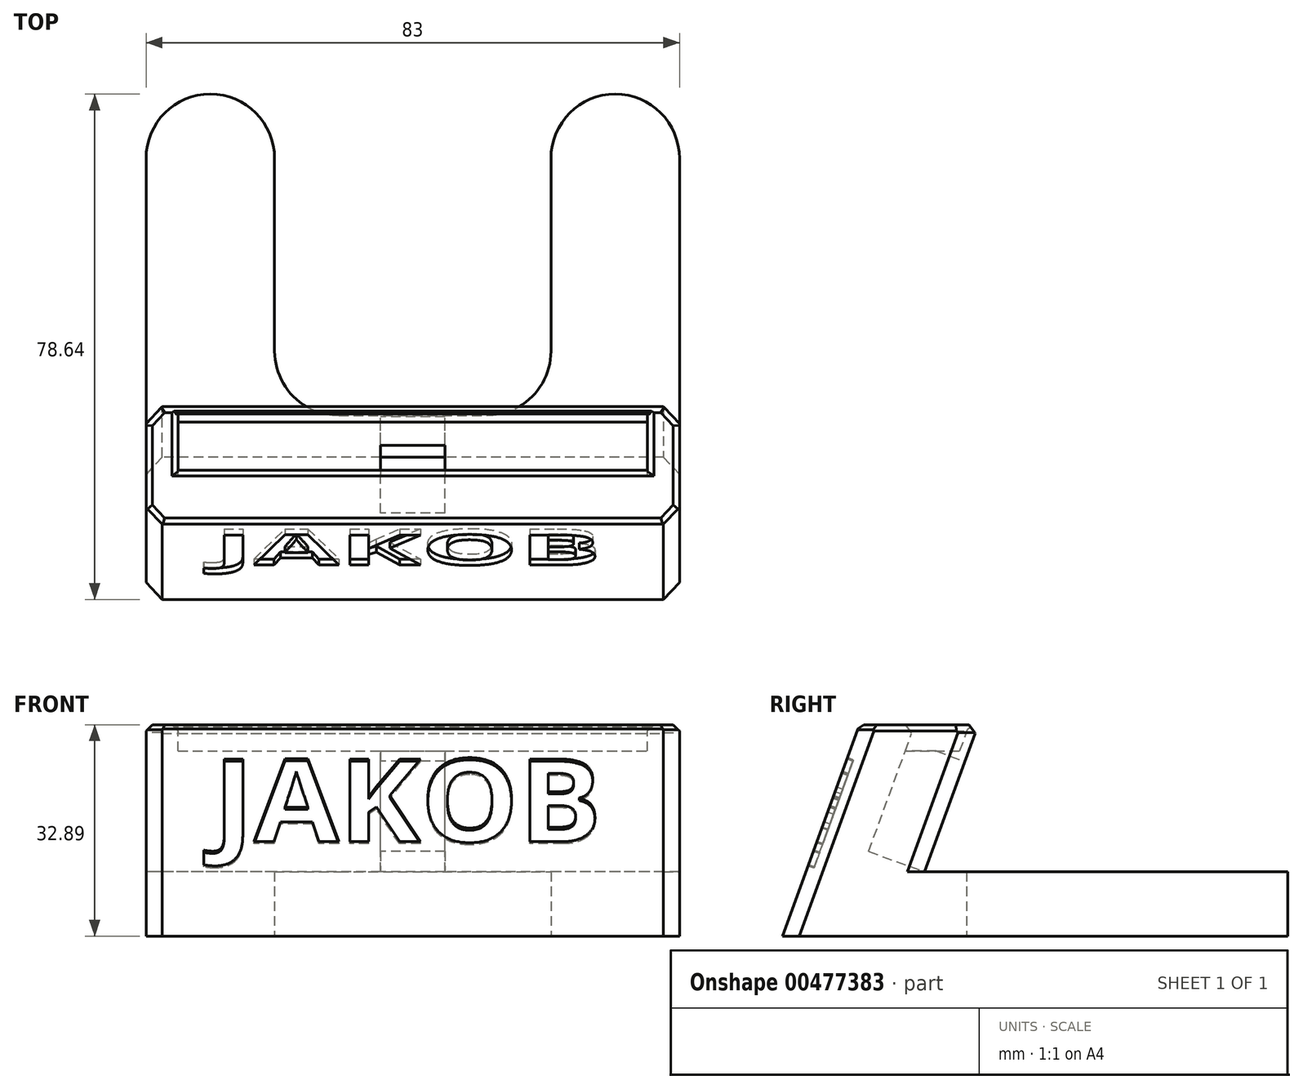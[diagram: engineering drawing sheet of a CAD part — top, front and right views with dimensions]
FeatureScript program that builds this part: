
annotation { "Feature Type Name" : "Feature", "Feature Type Description" : "" }
export const myFeature = defineFeature(function(context is Context, id is Id, definition is map)
    precondition{}
    {
        {
            var Q0;
            Q0=qCreatedBy(makeId("Top.planeOp"),FACE);
            var sketch = newSketch(context, id + "F0", { "sketchPlane" : qUnion([Q0])});
            skLineSegment(sketch, "E0.bottom", {"start": v(0, 0) * mm, "end": v(83, 0) * mm});
            skLineSegment(sketch, "E0.left", {"start": v(0, 0) * mm, "end": v(0, 75) * mm});
            skLineSegment(sketch, "E0.right", {"start": v(83, 0) * mm, "end": v(83, 75) * mm});
            skLineSegment(sketch, "E1", {"start": v(0, 75) * mm, "end": v(20, 75) * mm});
            skLineSegment(sketch, "E2", {"start": v(20, 75) * mm, "end": v(20, 25) * mm});
            skLineSegment(sketch, "E3", {"start": v(20, 25) * mm, "end": v(63, 25) * mm});
            skLineSegment(sketch, "E4", {"start": v(63, 25) * mm, "end": v(63, 75) * mm});
            skLineSegment(sketch, "E5", {"start": v(63, 75) * mm, "end": v(83, 75) * mm});
            skSolve(sketch);
        }
        {
            var Q0;
            Q0 = qSketchRegion(id + "F0", true);
            extrude(context, id + "F1", {"entities" : qUnion([Q0]), "depth" : 10 * mm});
        }
        {
            var Q0;
            Q0=makeQuery(id+"F1.opExtrude","CAP_FACE",FACE,{"disambiguationData":[OSD([sQuery(id+"F0.wireOp",EDGE,"E0.bottom"),sQuery(id+"F0.wireOp",EDGE,"E0.left"),sQuery(id+"F0.wireOp",EDGE,"E0.right"),sQuery(id+"F0.wireOp",EDGE,"E1"),sQuery(id+"F0.wireOp",EDGE,"E2"),sQuery(id+"F0.wireOp",EDGE,"E3"),sQuery(id+"F0.wireOp",EDGE,"E4"),sQuery(id+"F0.wireOp",EDGE,"E5")])],"isStart":false});
            var sketch = newSketch(context, id + "F2", { "sketchPlane" : qUnion([Q0])});
            skLineSegment(sketch, "E6.bottom", {"start": v(83, 0) * mm, "end": v(0, 0) * mm});
            skLineSegment(sketch, "E6.top", {"start": v(83, 18.5) * mm, "end": v(0, 18.5) * mm});
            skLineSegment(sketch, "E6.left", {"start": v(83, 0) * mm, "end": v(83, 18.5) * mm});
            skLineSegment(sketch, "E6.right", {"start": v(0, 0) * mm, "end": v(0, 18.5) * mm});
            skSolve(sketch);
        }
        {
            var Q0;
            Q0=qCreatedBy(makeId("Right.planeOp"),FACE);
            var sketch = newSketch(context, id + "F3", { "sketchPlane" : qUnion([Q0])});
            skLineSegment(sketch, "E7", {"start": v(0, 0) * mm, "end": v(11.97, 32.89) * mm});
            skSolve(sketch);
        }
        {
            var Q0;
            Q0 = qSketchRegion(id + "F2", true);
            var Q1;
            Q1=sQuery(id+"F3.wireOp",EDGE,"E7");
            sweep(context, id + "F4", {"operationType" : NewBodyOperationType.ADD, "profiles" : qUnion([Q0]), "path" : qUnion([Q1])});
        }
        {
            var Q0;
            Q0=makeQuery(id+"F4.opSweep","CAP_FACE",FACE,{"disambiguationData":[OSD([sQuery(id+"F2.wireOp",EDGE,"E6.bottom"),sQuery(id+"F2.wireOp",EDGE,"E6.top"),sQuery(id+"F2.wireOp",EDGE,"E6.left"),sQuery(id+"F2.wireOp",EDGE,"E6.right"),sQuery(id+"F3.wireOp",VERTEX,"E7.end")])],"isStart":false});
            var sketch = newSketch(context, id + "F5", { "sketchPlane" : qUnion([Q0])});
            skLineSegment(sketch, "E8.bottom", {"start": v(5, 16.97) * mm, "end": v(78, 16.97) * mm});
            skLineSegment(sketch, "E8.top", {"start": v(5, 25.47) * mm, "end": v(78, 25.47) * mm});
            skLineSegment(sketch, "E8.left", {"start": v(5, 16.97) * mm, "end": v(5, 25.47) * mm});
            skLineSegment(sketch, "E8.right", {"start": v(78, 16.97) * mm, "end": v(78, 25.47) * mm});
            skPoint(sketch, "E8.middle", {"position": v(41.5, 21.22) * mm});
            skPoint(sketch, "E8.middle.positionSnap0", {"position": v(41.5, 30.47) * mm});
            skPoint(sketch, "E8.middle.positionSnap1", {"position": v(83, 21.22) * mm});
            skPoint(sketch, "E8.centerSnap0", {"position": v(41.5, 30.47) * mm});
            skPoint(sketch, "E8.centerSnap1", {"position": v(83, 21.22) * mm});
            skSolve(sketch);
        }
        {
            var Q0;
            Q0=makeQuery(id+"F4.boolean.opBoolean","MERGE",FACE,{"derivedFrom":[makeQuery(id+"F1.opExtrude","SWEPT_FACE",FACE,{"disambiguationData":[OSD([sQuery(id+"F0.wireOp",EDGE,"E0.left")])]}),makeQuery(id+"F4.opSweep","SWEPT_FACE",FACE,{"disambiguationData":[OSD([sQuery(id+"F2.wireOp",EDGE,"E6.right"),sQuery(id+"F3.wireOp",EDGE,"E7")])]})]});
            var sketch = newSketch(context, id + "F6", { "sketchPlane" : qUnion([Q0])});
            skLineSegment(sketch, "E9", {"start": v(-11.97, 42.89) * mm, "end": v(-6.84, 28.8) * mm});
            skSolve(sketch);
        }
        {
            var Q0;
            Q0 = qSketchRegion(id + "F5", true);
            var Q1;
            Q1=sQuery(id+"F6.wireOp",EDGE,"E9");
            sweep(context, id + "F7", {"operationType" : NewBodyOperationType.REMOVE, "profiles" : qUnion([Q0]), "path" : qUnion([Q1])});
        }
        {
            var Q0;
            Q0=makeQuery(id+"F4.opSweep","SWEPT_FACE",FACE,{"disambiguationData":[OSD([sQuery(id+"F2.wireOp",EDGE,"E6.bottom"),sQuery(id+"F3.wireOp",EDGE,"E7")])]});
            var sketch = newSketch(context, id + "F8", { "sketchPlane" : qUnion([Q0])});
            skLineSegment(sketch, "E10.bottom", {"start": v(15, 44.4) * mm, "end": v(68, 44.4) * mm});
            skLineSegment(sketch, "E10.top", {"start": v(15, 34.4) * mm, "end": v(68, 34.4) * mm});
            skLineSegment(sketch, "E10.left", {"start": v(15, 44.4) * mm, "end": v(15, 34.4) * mm});
            skLineSegment(sketch, "E10.right", {"start": v(68, 44.4) * mm, "end": v(68, 34.4) * mm});
            skSolve(sketch);
        }
        {
            var Q0;
            Q0=makeQuery(id+"F4.opSweep","CAP_FACE",FACE,{"disambiguationData":[OSD([sQuery(id+"F2.wireOp",EDGE,"E6.bottom"),sQuery(id+"F2.wireOp",EDGE,"E6.top"),sQuery(id+"F2.wireOp",EDGE,"E6.left"),sQuery(id+"F2.wireOp",EDGE,"E6.right"),sQuery(id+"F3.wireOp",VERTEX,"E7.end")])],"isStart":false});
            var sketch = newSketch(context, id + "F9", { "sketchPlane" : qUnion([Q0])});
            skLineSegment(sketch, "E11", {"start": v(15, 16.97) * mm, "end": v(15, 11.97) * mm});
            skSolve(sketch);
        }
        {
            var Q0;
            Q0 = qSketchRegion(id + "F8", true);
            var Q1;
            Q1=sQuery(id+"F9.wireOp",EDGE,"E11");
            sweep(context, id + "F10", {"operationType" : NewBodyOperationType.REMOVE, "profiles" : qUnion([Q0]), "path" : qUnion([Q1])});
        }
        {
            var Q0;
            Q0=makeQuery(id+"F4.opSweep","SWEPT_EDGE",EDGE,{"disambiguationData":[OSD([sQuery(id+"F2.wireOp",EDGE,"E6.bottom"),sQuery(id+"F2.wireOp",EDGE,"E6.right"),sQuery(id+"F3.wireOp",EDGE,"E7")])]});
            var Q1;
            Q1=makeQuery(id+"F4.opSweep","SWEPT_EDGE",EDGE,{"disambiguationData":[OSD([sQuery(id+"F0.wireOp",EDGE,"E0.left"),sQuery(id+"F2.wireOp",EDGE,"E6.top"),sQuery(id+"F2.wireOp",EDGE,"E6.right"),sQuery(id+"F3.wireOp",EDGE,"E7")])]});
            var Q2;
            Q2=makeQuery(id+"F4.opSweep","SWEPT_EDGE",EDGE,{"disambiguationData":[OSD([sQuery(id+"F2.wireOp",EDGE,"E6.bottom"),sQuery(id+"F2.wireOp",EDGE,"E6.left"),sQuery(id+"F3.wireOp",EDGE,"E7")])]});
            var Q3;
            Q3=makeQuery(id+"F4.opSweep","SWEPT_EDGE",EDGE,{"disambiguationData":[OSD([sQuery(id+"F0.wireOp",EDGE,"E0.right"),sQuery(id+"F2.wireOp",EDGE,"E6.top"),sQuery(id+"F2.wireOp",EDGE,"E6.left"),sQuery(id+"F3.wireOp",EDGE,"E7")])]});
            chamfer(context, id + "F11", {"entities" : qUnion([Q0, Q1, Q2, Q3]), "width" : 2.5 * mm, "tangentPropagation" : true});
        }
        {
            var Q0;
            Q0=makeQuery(id+"F1.opExtrude","SWEPT_EDGE",EDGE,{"disambiguationData":[OSD([sQuery(id+"F0.wireOp",EDGE,"E1"),sQuery(id+"F0.wireOp",EDGE,"E2")])]});
            var Q1;
            Q1=makeQuery(id+"F1.opExtrude","SWEPT_EDGE",EDGE,{"disambiguationData":[OSD([sQuery(id+"F0.wireOp",EDGE,"E0.left"),sQuery(id+"F0.wireOp",EDGE,"E1")])]});
            var Q2;
            Q2=makeQuery(id+"F1.opExtrude","SWEPT_EDGE",EDGE,{"disambiguationData":[OSD([sQuery(id+"F0.wireOp",EDGE,"E4"),sQuery(id+"F0.wireOp",EDGE,"E5")])]});
            var Q3;
            Q3=makeQuery(id+"F1.opExtrude","SWEPT_EDGE",EDGE,{"disambiguationData":[OSD([sQuery(id+"F0.wireOp",EDGE,"E0.right"),sQuery(id+"F0.wireOp",EDGE,"E5")])]});
            var Q4;
            Q4=makeQuery(id+"F1.opExtrude","SWEPT_EDGE",EDGE,{"disambiguationData":[OSD([sQuery(id+"F0.wireOp",EDGE,"E3"),sQuery(id+"F0.wireOp",EDGE,"E4")])]});
            var Q5;
            Q5=makeQuery(id+"F1.opExtrude","SWEPT_EDGE",EDGE,{"disambiguationData":[OSD([sQuery(id+"F0.wireOp",EDGE,"E2"),sQuery(id+"F0.wireOp",EDGE,"E3")])]});
            fillet(context, id + "F12", {"entities" : qUnion([Q0, Q1, Q2, Q3, Q4, Q5]), "radius" : 10 * mm, "tangentPropagation" : true, "allowEdgeOverflow" : false});
        }
        {
            var Q0;
            Q0=makeQuery(id+"F4.opSweep","SWEPT_FACE",FACE,{"disambiguationData":[OSD([sQuery(id+"F2.wireOp",EDGE,"E6.bottom"),sQuery(id+"F3.wireOp",EDGE,"E7")])]});
            var sketch = newSketch(context, id + "F13", { "sketchPlane" : qUnion([Q0])});
            skText(sketch, "E12", { "text": "JAKOB", "fontName": "OpenSans-Bold.ttf"});
            skLineSegment(sketch, "E13", {"start": v(41.5, 14.4) * mm, "end": v(41.5, 9.4) * mm, "construction": true});
            const initialGuessF13  = {"E12": [0.01043, 0.0144, 1, 0, 0.0138]};
            skSetInitialGuess(sketch, initialGuessF13);
            skSolve(sketch);
        }
        {
            var Q0;
            Q0 = qSketchRegion(id + "F13", true);
            extrude(context, id + "F14", {"entities" : qUnion([Q0]), "operationType" : NewBodyOperationType.REMOVE, "oppositeDirection" : true, "depth" : 1 * mm});
        }
        {
            var Q0;
            Q0=makeQuery(id+"F4.opSweep","SWEPT_FACE",FACE,{"disambiguationData":[OSD([sQuery(id+"F2.wireOp",EDGE,"E6.top"),sQuery(id+"F3.wireOp",EDGE,"E7")])]});
            var sketch = newSketch(context, id + "F15", { "sketchPlane" : qUnion([Q0])});
            skLineSegment(sketch, "E14.bottom", {"start": v(-46.5, 15.72) * mm, "end": v(-36.5, 15.72) * mm});
            skLineSegment(sketch, "E14.top", {"start": v(-46.5, 34.01) * mm, "end": v(-36.5, 34.01) * mm});
            skLineSegment(sketch, "E14.left", {"start": v(-36.5, 15.72) * mm, "end": v(-36.5, 34.01) * mm});
            skLineSegment(sketch, "E14.right", {"start": v(-46.5, 15.72) * mm, "end": v(-46.5, 34.01) * mm});
            skSolve(sketch);
        }
        {
            var Q0;
            Q0 = qSketchRegion(id + "F15", true);
            var Q1;
            Q1=makeQuery(id+"F7.boolean.opBoolean","COPY",FACE,{"derivedFrom":makeQuery(id+"F7.opSweep","SWEPT_FACE",FACE,{"disambiguationData":[OSD([sQuery(id+"F5.wireOp",EDGE,"E8.bottom"),sQuery(id+"F6.wireOp",EDGE,"E9")])]})});
            extrude(context, id + "F16", {"entities" : qUnion([Q0]), "operationType" : NewBodyOperationType.REMOVE, "endBound" : BoundingType.UP_TO_SURFACE, "oppositeDirection" : true, "endBoundEntityFace" : qUnion([Q1]), "depth" : 5 * mm});
        }
        {
            var Q0;
            Q0=makeQuery(id+"F4.opSweep","CAP_FACE",FACE,{"disambiguationData":[OSD([sQuery(id+"F2.wireOp",EDGE,"E6.bottom"),sQuery(id+"F2.wireOp",EDGE,"E6.top"),sQuery(id+"F2.wireOp",EDGE,"E6.left"),sQuery(id+"F2.wireOp",EDGE,"E6.right"),sQuery(id+"F3.wireOp",VERTEX,"E7.end")])],"isStart":false});
            chamfer(context, id + "F17", {"entities" : qUnion([Q0]), "width" : 1 * mm, "tangentPropagation" : true});
        }
    });
